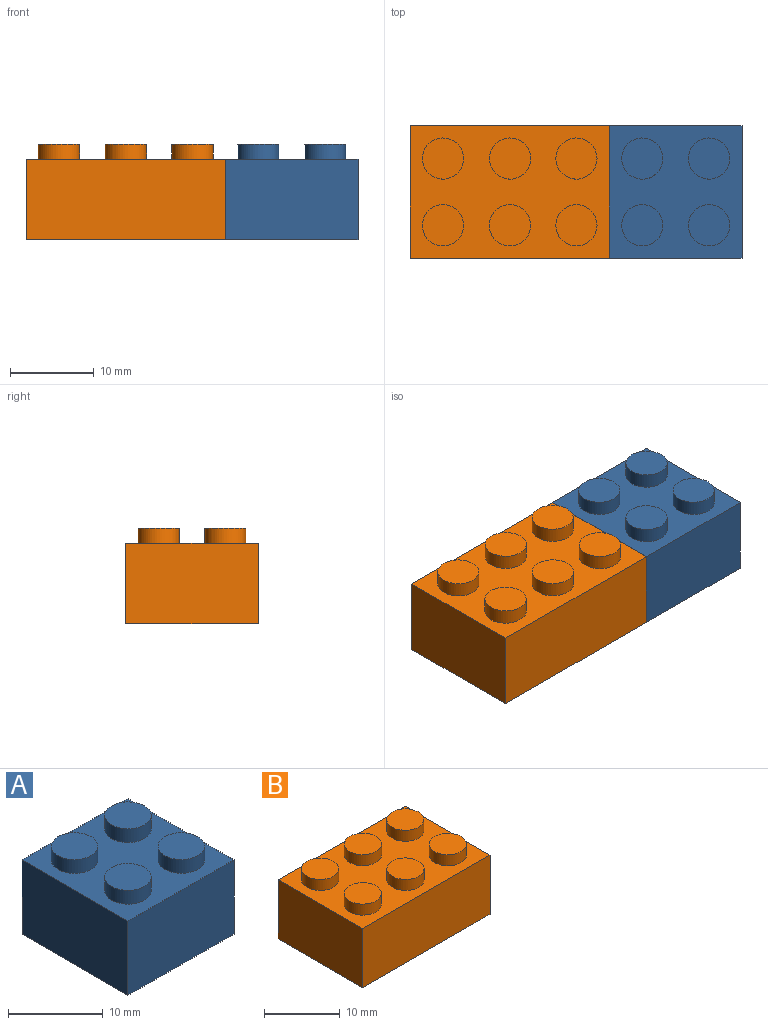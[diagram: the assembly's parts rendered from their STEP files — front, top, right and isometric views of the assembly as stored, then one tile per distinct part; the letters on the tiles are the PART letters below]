
ASSEMBLY  parts=2 mates=1
PART A: 23 faces, bbox 15.8x15.8x11.4 mm
  f0: plane 15.8x9.58mm, normal (-1,0,0), area 151.3mm2, adj f1,f3,f4,f5
  f1: plane 15.8x9.58mm, normal (0,-1,0), area 151.3mm2, adj f0,f2,f4,f5
  f2: plane 15.8x9.58mm, normal (1,0,0), area 151.3mm2, adj f1,f3,f4,f5
  f3: plane 15.8x9.58mm, normal (0,1,0), area 151.3mm2, adj f0,f2,f4,f5
  f4: plane 15.8x15.8mm, normal (0,0,1), area 174.1mm2, adj f0,f1,f2,f3,f6,f8,f10,f12
  f5: plane 15.8x15.8mm, normal (0,0,-1), area 34.1mm2, adj f0,f1,f2,f3,f14,f15,f16,f17
  f6: cylinder r=2.45mm len=4.91mm, axis (0,0,-1), area 27.4mm2, adj f4,f7
  f7: plane 4.91x4.91mm, normal (0,0,1), area 18.9mm2, adj f6
  f8: cylinder r=2.45mm len=4.9mm, axis (0,0,-1), area 27.4mm2, adj f4,f9
  f9: plane 4.9x4.9mm, normal (0,0,1), area 18.9mm2, adj f8
  f10: cylinder r=2.45mm len=4.9mm, axis (0,0,-1), area 27.4mm2, adj f4,f11
  f11: plane 4.9x4.9mm, normal (0,0,1), area 18.9mm2, adj f10
  f12: cylinder r=2.45mm len=4.9mm, axis (0,0,-1), area 27.4mm2, adj f4,f13
  f13: plane 4.9x4.9mm, normal (0,0,1), area 18.9mm2, adj f12
  f14: plane 14.69x8.33mm, normal (1,0,0), area 122.4mm2, adj f5,f15,f17,f18
  f15: plane 14.67x8.33mm, normal (0,-1,0), area 122.2mm2, adj f5,f14,f16,f18
  f16: plane 14.69x8.33mm, normal (-1,0,0), area 122.4mm2, adj f5,f15,f17,f18
  f17: plane 14.67x8.33mm, normal (0,1,0), area 122.2mm2, adj f5,f14,f16,f18
  f18: plane 14.69x14.67mm, normal (0,0,-1), area 183.3mm2, adj f14,f15,f16,f17,f19
  f19: cylinder r=3.2mm len=8.33mm, axis (0,0,-1), area 167.5mm2, adj f18,f20
  f20: plane 6.4x6.4mm, normal (0,0,-1), area 7.7mm2, adj f19,f21
  f21: cylinder r=2.79mm len=8.33mm, axis (0,0,-1), area 146.3mm2, adj f20,f22
  f22: plane 5.59x5.59mm, normal (0,0,-1), area 24.5mm2, adj f21
PART B: 31 faces, bbox 23.7x15.8x11.3 mm
  f0: plane 15.8x9.55mm, normal (-1,0,0), area 150.9mm2, adj f1,f3,f4,f5
  f1: plane 23.75x9.55mm, normal (0,-1,0), area 226.8mm2, adj f0,f2,f4,f5
  f2: plane 15.8x9.55mm, normal (1,0,0), area 150.9mm2, adj f1,f3,f4,f5
  f3: plane 23.75x9.55mm, normal (0,1,0), area 226.8mm2, adj f0,f2,f4,f5
  f4: plane 23.75x15.8mm, normal (0,0,1), area 262mm2, adj f0,f1,f2,f3,f6,f8,f10,f12
  f5: plane 23.75x15.8mm, normal (0,0,-1), area 46.7mm2, adj f0,f1,f2,f3,f18,f19,f20,f21
  f6: cylinder r=2.45mm len=4.9mm, axis (0,0,-1), area 27.4mm2, adj f4,f7
  f7: plane 4.9x4.9mm, normal (0,0,1), area 18.9mm2, adj f6
  f8: cylinder r=2.45mm len=4.9mm, axis (0,0,-1), area 27.4mm2, adj f4,f9
  f9: plane 4.9x4.9mm, normal (0,0,1), area 18.9mm2, adj f8
  f10: cylinder r=2.45mm len=4.9mm, axis (0,0,-1), area 27.4mm2, adj f4,f11
  f11: plane 4.9x4.9mm, normal (0,0,1), area 18.9mm2, adj f10
  f12: cylinder r=2.45mm len=4.9mm, axis (0,0,-1), area 27.4mm2, adj f4,f13
  f13: plane 4.9x4.9mm, normal (0,0,1), area 18.9mm2, adj f12
  f14: cylinder r=2.45mm len=4.9mm, axis (0,0,-1), area 27.4mm2, adj f4,f15
  f15: plane 4.9x4.9mm, normal (0,0,1), area 18.9mm2, adj f14
  f16: cylinder r=2.45mm len=4.9mm, axis (0,0,-1), area 27.4mm2, adj f4,f17
  f17: plane 4.9x4.9mm, normal (0,0,1), area 18.9mm2, adj f16
  f18: plane 14.58x8.33mm, normal (1,0,0), area 121.5mm2, adj f5,f19,f21,f22
  f19: plane 22.53x8.33mm, normal (0,-1,0), area 187.7mm2, adj f5,f18,f20,f22
  f20: plane 14.58x8.33mm, normal (-1,0,0), area 121.5mm2, adj f5,f19,f21,f22
  f21: plane 22.53x8.33mm, normal (0,1,0), area 187.7mm2, adj f5,f18,f20,f22
  f22: plane 22.53x14.58mm, normal (0,0,-1), area 262.6mm2, adj f18,f19,f20,f21,f23,f25
  f23: cylinder r=3.24mm len=8.33mm, axis (0,0,-1), area 169.5mm2, adj f22,f24
  f24: plane 6.48x6.48mm, normal (0,0,-1), area 8.4mm2, adj f23,f27
  f25: cylinder r=3.24mm len=8.33mm, axis (0,0,-1), area 169.5mm2, adj f22,f26
  f26: plane 6.48x6.48mm, normal (0,0,-1), area 8.4mm2, adj f25,f29
  f27: cylinder r=2.79mm len=8.33mm, axis (0,0,-1), area 146.3mm2, adj f24,f28
  f28: plane 5.59x5.59mm, normal (0,0,-1), area 24.5mm2, adj f27
  f29: cylinder r=2.79mm len=8.33mm, axis (0,0,-1), area 146.3mm2, adj f26,f30
  f30: plane 5.59x5.59mm, normal (0,0,-1), area 24.5mm2, adj f29
PLACE A t=(26.71,15.03,-1.47)mm
PLACE B t=(6.94,15.03,-6.25)mm
MATE planar B.f2 <-> A.f0  axis (1,0,0) through (18.81,15.03,-1.47)mm
